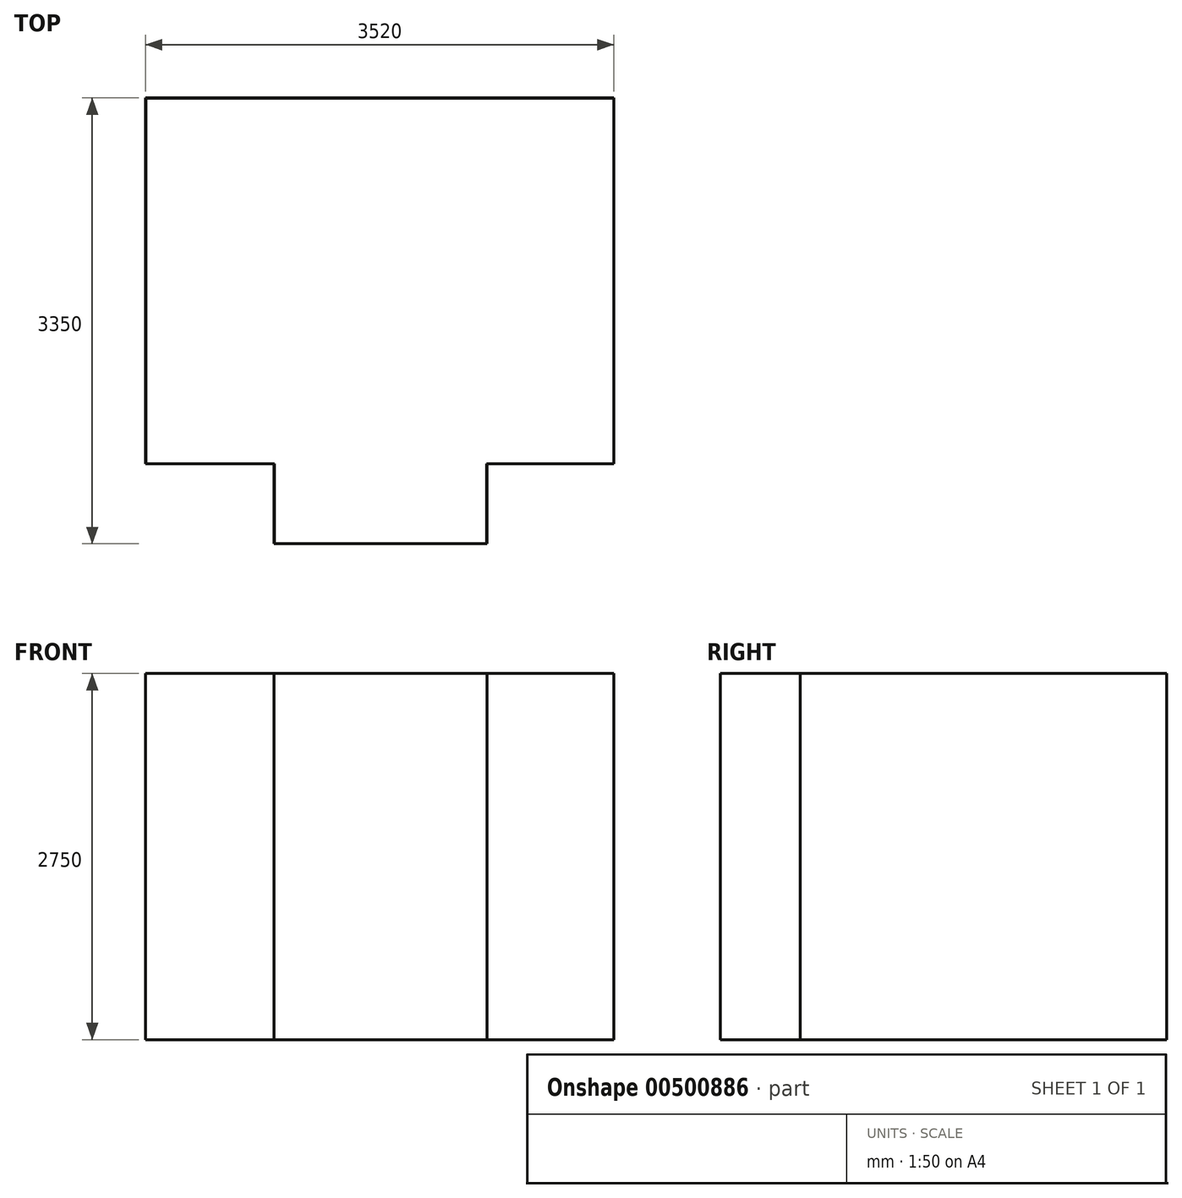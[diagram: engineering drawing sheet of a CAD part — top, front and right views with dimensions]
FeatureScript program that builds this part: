
annotation { "Feature Type Name" : "Feature", "Feature Type Description" : "" }
export const myFeature = defineFeature(function(context is Context, id is Id, definition is map)
    precondition{}
    {
        {
            var Q0;
            Q0=qCreatedBy(makeId("Top.planeOp"),FACE);
            var sketch = newSketch(context, id + "F0", { "sketchPlane" : qUnion([Q0])});
            skLineSegment(sketch, "E0.bottom", {"start": v(0, 0) * mm, "end": v(966.17, 0) * mm});
            skLineSegment(sketch, "E0.top", {"start": v(0, 2750) * mm, "end": v(3520, 2750) * mm});
            skLineSegment(sketch, "E0.left", {"start": v(0, 0) * mm, "end": v(0, 2750) * mm});
            skLineSegment(sketch, "E0.right", {"start": v(3520, 0) * mm, "end": v(3520, 2750) * mm});
            skLineSegment(sketch, "E1.top", {"start": v(966.17, -600) * mm, "end": v(2566.17, -600) * mm});
            skLineSegment(sketch, "E1.left", {"start": v(966.17, 0) * mm, "end": v(966.17, -600) * mm});
            skLineSegment(sketch, "E1.right", {"start": v(2566.17, 0) * mm, "end": v(2566.17, -600) * mm});
            skLineSegment(sketch, "E2.trimOffspring", {"start": v(2566.17, 0) * mm, "end": v(3520, 0) * mm});
            skSolve(sketch);
        }
        {
            var Q0;
            Q0 = qSketchRegion(id + "F0", true);
            extrude(context, id + "F1", {"entities" : qUnion([Q0]), "depth" : 2750 * mm, "offsetDistance" : 25 * mm});
        }
        {
            var Q0;
            Q0=makeQuery(id+"F1.opExtrude","CAP_FACE",FACE,{"disambiguationData":[OSD([sQuery(id+"F0.wireOp",EDGE,"E0.bottom"),sQuery(id+"F0.wireOp",EDGE,"E0.top"),sQuery(id+"F0.wireOp",EDGE,"E0.left"),sQuery(id+"F0.wireOp",EDGE,"E0.right"),sQuery(id+"F0.wireOp",EDGE,"E1.top"),sQuery(id+"F0.wireOp",EDGE,"E1.left"),sQuery(id+"F0.wireOp",EDGE,"E1.right"),sQuery(id+"F0.wireOp",EDGE,"E2.trimOffspring")])],"isStart":false});
            shell(context, id + "F2", {"entities" : qUnion([Q0]), "thickness" : 2.5 * mm});
        }
    });
